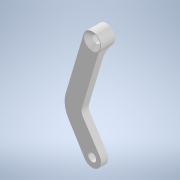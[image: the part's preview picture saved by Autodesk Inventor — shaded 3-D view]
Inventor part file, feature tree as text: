
AUTODESK INVENTOR PART (.ipt)
format: ipt  version: 2022 (Build 260153000, 153)  size: 182,784 bytes
history: native  units: mm
features: other x5, reference x5, extrude x2, fillet x2, sketch x2, chamfer x1, projected_geometry x1
ambient origin geometry x8: Origin, YZ Plane, XZ Plane, XY Plane, X Axis, Y Axis, Z Axis, Center Point
bodies: Body1 (feature_tree)
feature tree (18):
  other  "Твердое тело1"
  extrude  "Выдавливание1"  Depth=2.0mm TaperAngle=0.0deg
  extrude  "Выдавливание2"  Depth=28.18mm
  fillet  "Сопряжение3"  Radius=2.2mm
  fillet  "Сопряжение4"  Radius=2.2mm
  chamfer  "Фаска1"  Distance=5.0mm
  sketch  "Эскиз1"
  reference  "Ссылка1"
  reference  "Ссылка2"
  reference  "Ссылка3"
  reference  "Ссылка4"
  reference  "Ссылка5"
  sketch  "Эскиз2"
  projected_geometry  "Спроецированная петля1"
  other  "<userpath>\Documents\Git\MZCAT_2024\MZCAT_2.iam"
  other  "MZCAT_2.iam"
  other  "lidar_krestovina:1"
  other  "lidar_shatun_main:1"
